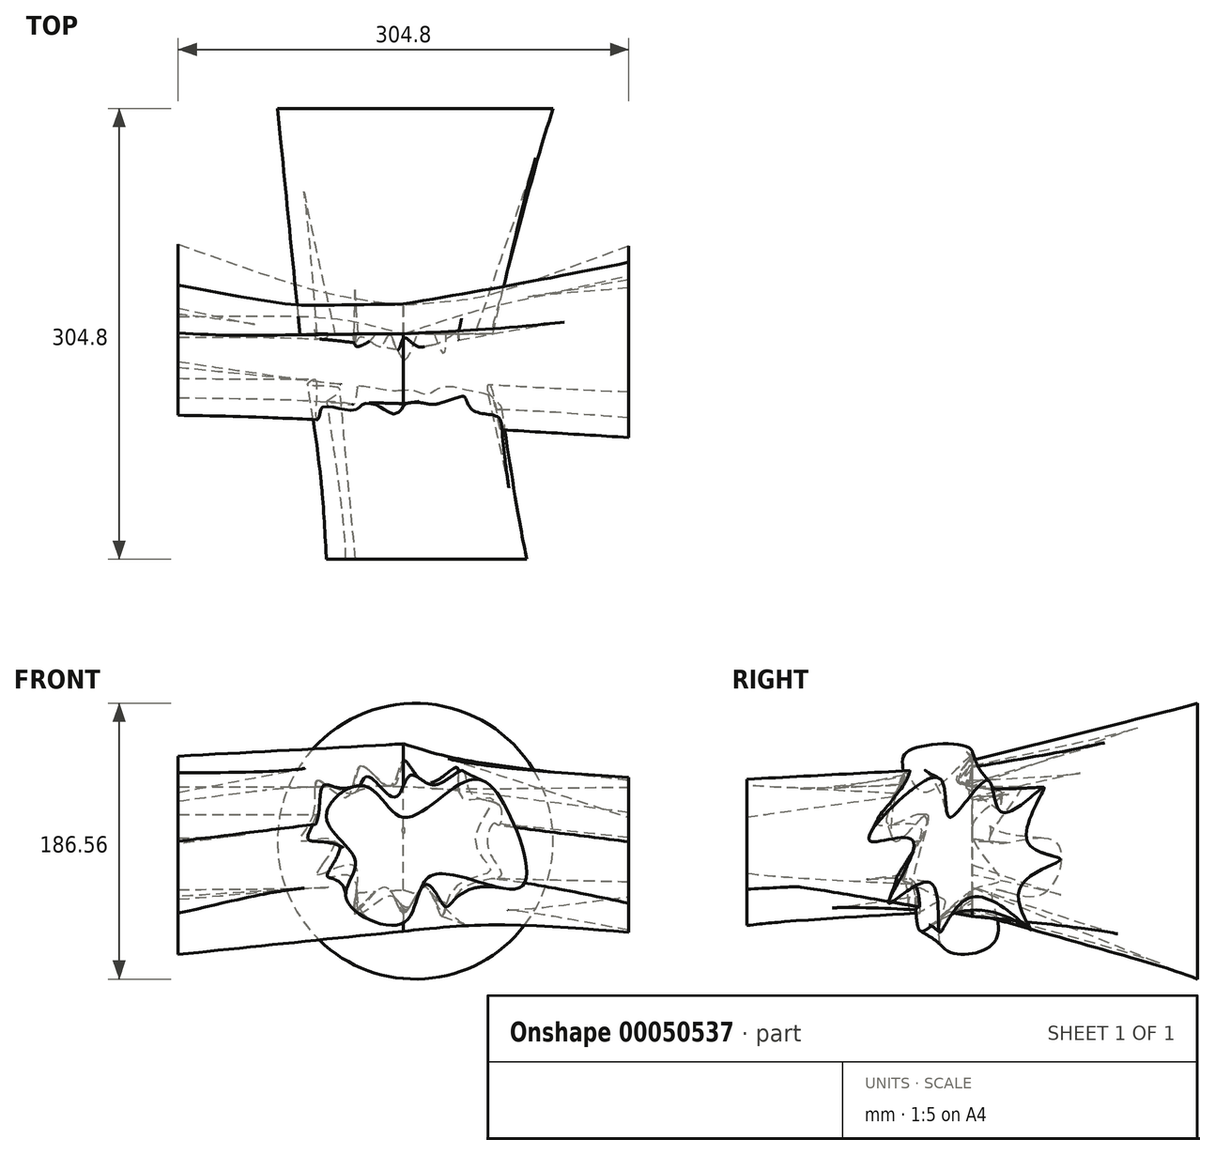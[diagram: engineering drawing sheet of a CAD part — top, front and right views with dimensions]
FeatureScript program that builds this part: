
annotation { "Feature Type Name" : "Feature", "Feature Type Description" : "" }
export const myFeature = defineFeature(function(context is Context, id is Id, definition is map)
    precondition{}
    {
        {
            var Q0;
            Q0=qCreatedBy(makeId("Front.planeOp"),FACE);
            var sketch = newSketch(context, id + "F0", { "sketchPlane" : qUnion([Q0])});
            skFitSpline(sketch, "E0", {"points": [v(-61.25, 17.1) * mm, v(-57.8, 41.3) * mm, v(-38.26, 29.71) * mm, v(-28.9, 51.08) * mm, v(-8.95, 37.24) * mm, v(0, 54.54) * mm, v(15.87, 39.48) * mm, v(36.22, 49.86) * mm, v(39.07, 29.71) * mm, v(60.24, 29.1) * mm, v(48.23, 0) * mm, v(58.81, -19.74) * mm, v(33.98, -31.95) * mm, v(25.64, -50.67) * mm, v(14.45, -31.14) * mm, v(0, -48.43) * mm, v(-12.2, -31.34) * mm, v(-32.97, -46.4) * mm, v(-33.17, -16.9) * mm, v(-58.4, -22.59) * mm, v(-46.6, 0) * mm, v(-69.4, 0) * mm, v(-61.25, 17.1) * mm]});
            skSolve(sketch);
        }
        {
            var Q0;
            Q0=qCreatedBy(makeId("Front.planeOp"),FACE);
            cPlane(context, id + "F1", {"entities" : qUnion([Q0]), "cplaneType" : CPlaneType.OFFSET, "offset" : 152.4 * mm, "width" : 152.4 * mm, "height" : 152.4 * mm});
        }
        {
            var Q0;
            Q0=qCreatedBy(makeId("Right.planeOp"),FACE);
            cPlane(context, id + "F2", {"entities" : qUnion([Q0]), "cplaneType" : CPlaneType.OFFSET, "offset" : 152.4 * mm, "width" : 152.4 * mm, "height" : 152.4 * mm});
        }
        {
            var Q0;
            Q0=qCreatedBy(id+"F2.planeOp",FACE);
            var sketch = newSketch(context, id + "F3", { "sketchPlane" : qUnion([Q0])});
            skFitSpline(sketch, "E1", {"points": [v(-44.74, 31.75) * mm, v(-20.4, 40.4) * mm, v(-15.06, 16.15) * mm, v(10.33, 41.12) * mm, v(20.17, 19.44) * mm, v(48.33, 36.6) * mm, v(37.23, 0) * mm, v(59.38, -12.22) * mm, v(31.74, -32.66) * mm, v(39.6, -60.1) * mm, v(0, -37.71) * mm, v(-22.22, -61.54) * mm, v(-28.76, -28.07) * mm, v(-56.77, -41.9) * mm, v(-40.03, 0) * mm, v(-68.93, 0) * mm, v(-44.74, 31.75) * mm]});
            skSolve(sketch);
        }
        {
            var Q0;
            Q0=qCreatedBy(id+"F1.planeOp",FACE);
            var sketch = newSketch(context, id + "F4", { "sketchPlane" : qUnion([Q0])});
            skFitSpline(sketch, "E2", {"points": [v(-52.2, 16.61) * mm, v(-26.3, 37.25) * mm, v(0, 16.06) * mm, v(44.66, 41.38) * mm, v(71.28, 18.85) * mm, v(78.47, -31.49) * mm, v(18.87, -23.27) * mm, v(0, -55.23) * mm, v(-38.6, -39.19) * mm, v(-32.6, -13.38) * mm, v(-52.2, 16.61) * mm]});
            skSolve(sketch);
        }
        {
            var Q0;
            Q0=makeQuery(id+"F4.imprint","IMPRINT",FACE,{"disambiguationData":[TD([[makeQuery(id+"F4.imprint","IMPRINT",EDGE,{"derivedFrom":sQuery(id+"F4.wireOp",EDGE,"E2")}),-1.0]])]});
            var Q1;
            Q1=makeQuery(id+"F0.imprint","IMPRINT",FACE,{"disambiguationData":[TD([[makeQuery(id+"F0.imprint","IMPRINT",EDGE,{"derivedFrom":sQuery(id+"F0.wireOp",EDGE,"E0")}),-1.0]])]});
            loft(context, id + "F5", {"sheetProfilesArray" : [{ "sheetProfileEntities" : qUnion([Q0]) }, { "sheetProfileEntities" : qUnion([Q1]) }]});
        }
        {
            var Q0;
            Q0=qCreatedBy(makeId("Right.planeOp"),FACE);
            cPlane(context, id + "F6", {"entities" : qUnion([Q0]), "cplaneType" : CPlaneType.OFFSET, "offset" : 152.4 * mm, "oppositeDirection" : true, "width" : 152.4 * mm, "height" : 152.4 * mm});
        }
        {
            var Q0;
            Q0=qCreatedBy(makeId("Right.planeOp"),FACE);
            var sketch = newSketch(context, id + "F7", { "sketchPlane" : qUnion([Q0])});
            skFitSpline(sketch, "E3", {"points": [v(-47.65, 40.37) * mm, v(-60.37, 19.6) * mm, v(-31.1, 15.54) * mm, v(-52.67, -19.95) * mm, v(-42.13, -29.94) * mm, v(-35.12, -60.73) * mm, v(0, -32.96) * mm, v(19.05, -25.5) * mm, v(0, 9.57) * mm, v(20.04, 32.85) * mm, v(-11.3, 40.79) * mm, v(0, 60.73) * mm, v(-44.39, 60.21) * mm, v(-47.65, 40.37) * mm]});
            skSolve(sketch);
        }
        {
            var Q0;
            Q0=qCreatedBy(id+"F6.planeOp",FACE);
            var sketch = newSketch(context, id + "F8", { "sketchPlane" : qUnion([Q0])});
            skFitSpline(sketch, "E4", {"points": [v(-45.62, 46.07) * mm, v(-52.56, 0) * mm, v(-30.5, 18.1) * mm, v(-41.85, -48.02) * mm, v(-19.45, -39.3) * mm, v(-21.44, -69.85) * mm, v(15.83, -66.6) * mm, v(13.76, -33.4) * mm, v(46.41, -36.17) * mm, v(55.57, 0) * mm, v(11.82, 0) * mm, v(32.97, 36.57) * mm, v(0, 28.1) * mm, v(0, 57.39) * mm, v(-32.93, 33) * mm, v(-45.62, 46.07) * mm]});
            skSolve(sketch);
        }
        {
            var Q0;
            Q0=makeQuery(id+"F7.imprint","IMPRINT",FACE,{"disambiguationData":[TD([[makeQuery(id+"F7.imprint","IMPRINT",EDGE,{"derivedFrom":sQuery(id+"F7.wireOp",EDGE,"E3")}),1.0]])]});
            var Q1;
            Q1=makeQuery(id+"F3.imprint","IMPRINT",FACE,{"disambiguationData":[TD([[makeQuery(id+"F3.imprint","IMPRINT",EDGE,{"derivedFrom":sQuery(id+"F3.wireOp",EDGE,"E1")}),-1.0]])]});
            loft(context, id + "F9", {"sheetProfilesArray" : [{ "sheetProfileEntities" : qUnion([Q0]) }, { "sheetProfileEntities" : qUnion([Q1]) }]});
        }
        {
            var Q1;
            Q1=makeQuery(id+"F8.imprint","IMPRINT",FACE,{"disambiguationData":[TD([[makeQuery(id+"F8.imprint","IMPRINT",EDGE,{"derivedFrom":sQuery(id+"F8.wireOp",EDGE,"E4")}),1.0]])]});
            var Q2;
            Q2=makeQuery(id+"F9.opLoft","CAP_FACE",FACE,{"disambiguationData":[OSD([makeQuery(id+"F7.imprint","IMPRINT",FACE,{"disambiguationData":[TD([[makeQuery(id+"F7.imprint","IMPRINT",EDGE,{"derivedFrom":sQuery(id+"F7.wireOp",EDGE,"E3")}),1.0]])]})])],"isStart":true});
            loft(context, id + "F10", {"operationType" : NewBodyOperationType.ADD, "sheetProfilesArray" : [{ "sheetProfileEntities" : qUnion([Q1]) }, { "sheetProfileEntities" : qUnion([Q2]) }]});
        }
        {
            var Q0;
            Q0=qCreatedBy(makeId("Front.planeOp"),FACE);
            cPlane(context, id + "F11", {"entities" : qUnion([Q0]), "cplaneType" : CPlaneType.OFFSET, "offset" : 152.4 * mm, "oppositeDirection" : true, "width" : 152.4 * mm, "height" : 152.4 * mm});
        }
        {
            var Q0;
            Q0=qCreatedBy(id+"F11.planeOp",FACE);
            var sketch = newSketch(context, id + "F12", { "sketchPlane" : qUnion([Q0])});
            skCircle(sketch, "E5", {"center": v(7.99, 0) * mm, "radius": 93.28 * mm});
            skSolve(sketch);
        }
        {
            var Q0;
            Q0=makeQuery(id+"F0.imprint","IMPRINT",FACE,{"disambiguationData":[TD([[makeQuery(id+"F0.imprint","IMPRINT",EDGE,{"derivedFrom":sQuery(id+"F0.wireOp",EDGE,"E0")}),-1.0]])]});
            var Q1;
            Q1=makeQuery(id+"F12.imprint","IMPRINT",FACE,{"disambiguationData":[TD([[makeQuery(id+"F12.imprint","IMPRINT",EDGE,{"derivedFrom":sQuery(id+"F12.wireOp",EDGE,"E5")}),1.0]])]});
            loft(context, id + "F13", {"sheetProfilesArray" : [{ "sheetProfileEntities" : qUnion([Q0]) }, { "sheetProfileEntities" : qUnion([Q1]) }]});
        }
    });
